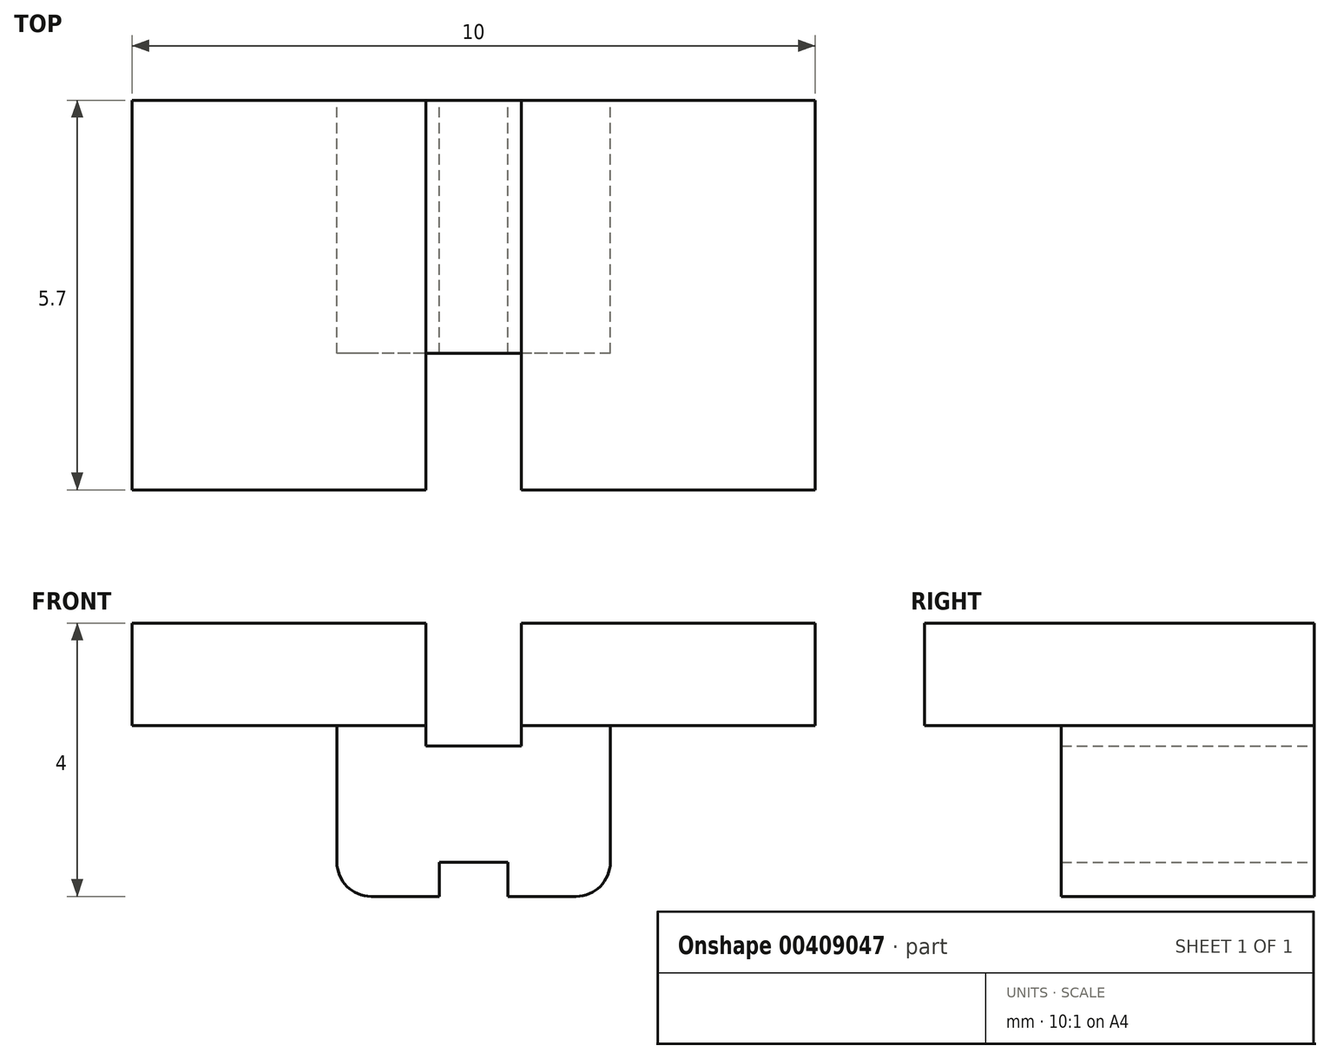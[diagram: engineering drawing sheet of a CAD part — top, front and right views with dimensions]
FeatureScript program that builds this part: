
annotation { "Feature Type Name" : "Feature", "Feature Type Description" : "" }
export const myFeature = defineFeature(function(context is Context, id is Id, definition is map)
    precondition{}
    {
        {
            var Q0;
            Q0=qCreatedBy(makeId("Top.planeOp"),FACE);
            var sketch = newSketch(context, id + "F0", { "sketchPlane" : qUnion([Q0])});
            skLineSegment(sketch, "E0.bottom", {"start": v(0.7, -0.75) * mm, "end": v(-0.7, -0.75) * mm});
            skLineSegment(sketch, "E0.top", {"start": v(0.7, 0.75) * mm, "end": v(-0.7, 0.75) * mm});
            skLineSegment(sketch, "E0.left", {"start": v(0.7, -0.75) * mm, "end": v(0.7, 0.75) * mm});
            skLineSegment(sketch, "E0.right", {"start": v(-0.7, -0.75) * mm, "end": v(-0.7, 0.75) * mm});
            skPoint(sketch, "E0.middle", {"position": v(0, 0) * mm});
            skLineSegment(sketch, "E1.bottom", {"start": v(2, -1.85) * mm, "end": v(-2, -1.85) * mm});
            skLineSegment(sketch, "E1.top", {"start": v(2, 1.85) * mm, "end": v(-2, 1.85) * mm});
            skLineSegment(sketch, "E1.left", {"start": v(2, -1.85) * mm, "end": v(2, 1.85) * mm});
            skLineSegment(sketch, "E1.right", {"start": v(-2, -1.85) * mm, "end": v(-2, 1.85) * mm});
            skLineSegment(sketch, "E2.bottom", {"start": v(5, -3.85) * mm, "end": v(-5, -3.85) * mm});
            skLineSegment(sketch, "E2.top", {"start": v(5, 1.85) * mm, "end": v(-5, 1.85) * mm});
            skLineSegment(sketch, "E2.left", {"start": v(5, -3.85) * mm, "end": v(5, 1.85) * mm});
            skLineSegment(sketch, "E2.right", {"start": v(-5, -3.85) * mm, "end": v(-5, 1.85) * mm});
            skPoint(sketch, "E2.middle", {"position": v(0, -1) * mm});
            skLineSegment(sketch, "E3", {"start": v(-0.7, -0.75) * mm, "end": v(-0.7, -3.85) * mm});
            skLineSegment(sketch, "E4", {"start": v(0.7, -0.75) * mm, "end": v(0.7, -3.85) * mm});
            skLineSegment(sketch, "E5", {"start": v(0.7, 0.75) * mm, "end": v(0.7, 1.85) * mm});
            skLineSegment(sketch, "E6", {"start": v(-0.7, 0.75) * mm, "end": v(-0.7, 1.85) * mm});
            skSolve(sketch);
        }
        {
            var Q0;
            Q0=makeQuery(id+"F0.imprint","IMPRINT",FACE,{"disambiguationData":[TD([[makeQuery(id+"F0.imprint","IMPRINT",EDGE,{"derivedFrom":sQuery(id+"F0.wireOp",EDGE,"E1.bottom")}),1.0]])]});
            var Q1;
            {var subQ0=sQuery(id+"F0.wireOp",EDGE,"E1.right");Q1=makeQuery(id+"F0.imprint","IMPRINT",FACE,{"disambiguationData":[TD([[makeQuery(id+"F0.imprint","IMPRINT",EDGE,{"derivedFrom":subQ0}),1.0]])]});}
            var Q2;
            {var subQ1=sQuery(id+"F0.wireOp",EDGE,"E1.left");Q2=makeQuery(id+"F0.imprint","IMPRINT",FACE,{"disambiguationData":[TD([[makeQuery(id+"F0.imprint","IMPRINT",EDGE,{"derivedFrom":subQ1}),-1.0]])]});}
            extrude(context, id + "F1", {"entities" : qUnion([Q0, Q1, Q2]), "oppositeDirection" : true, "depth" : 1.5 * mm});
        }
        {
            var Q0;
            Q0=makeQuery(id+"F0.imprint","IMPRINT",FACE,{"disambiguationData":[TD([[makeQuery(id+"F0.imprint","IMPRINT",EDGE,{"derivedFrom":sQuery(id+"F0.wireOp",EDGE,"E0.bottom")}),1.0]])]});
            var Q1;
            Q1=makeQuery(id+"F0.imprint","IMPRINT",FACE,{"disambiguationData":[TD([[makeQuery(id+"F0.imprint","IMPRINT",EDGE,{"derivedFrom":sQuery(id+"F0.wireOp",EDGE,"E0.bottom")}),-1.0]])]});
            var Q2;
            {var subQ6=sQuery(id+"F0.wireOp",EDGE,"E0.right");Q2=makeQuery(id+"F0.imprint","IMPRINT",FACE,{"disambiguationData":[TD([[makeQuery(id+"F0.imprint","IMPRINT",EDGE,{"derivedFrom":subQ6}),1.0]])]});}
            var Q3;
            Q3=makeQuery(id+"F0.imprint","IMPRINT",FACE,{"disambiguationData":[TD([[makeQuery(id+"F0.imprint","IMPRINT",EDGE,{"derivedFrom":sQuery(id+"F0.wireOp",EDGE,"E0.top")}),-1.0]])]});
            var Q4;
            {var subQ3=sQuery(id+"F0.wireOp",EDGE,"E0.left");Q4=makeQuery(id+"F0.imprint","IMPRINT",FACE,{"disambiguationData":[TD([[makeQuery(id+"F0.imprint","IMPRINT",EDGE,{"derivedFrom":subQ3}),-1.0]])]});}
            extrude(context, id + "F2", {"entities" : qUnion([Q0, Q1, Q2, Q3, Q4]), "operationType" : NewBodyOperationType.ADD, "oppositeDirection" : true, "depth" : 4 * mm});
        }
        {
            var Q0;
            Q0=makeQuery(id+"F0.imprint","IMPRINT",FACE,{"disambiguationData":[TD([[makeQuery(id+"F0.imprint","IMPRINT",EDGE,{"derivedFrom":sQuery(id+"F0.wireOp",EDGE,"E0.bottom")}),-1.0]])]});
            var Q1;
            Q1=makeQuery(id+"F0.imprint","IMPRINT",FACE,{"disambiguationData":[TD([[makeQuery(id+"F0.imprint","IMPRINT",EDGE,{"derivedFrom":sQuery(id+"F0.wireOp",EDGE,"E0.top")}),-1.0]])]});
            var Q2;
            {var subQ0=sQuery(id+"F0.wireOp",EDGE,"E0.bottom");Q2=makeQuery(id+"F0.imprint","IMPRINT",FACE,{"disambiguationData":[TD([[makeQuery(id+"F0.imprint","IMPRINT",EDGE,{"derivedFrom":subQ0}),1.0]])]});}
            var Q3;
            {var subQ0=sQuery(id+"F0.wireOp",EDGE,"E4");var subQ1=sQuery(id+"F0.wireOp",EDGE,"E1.bottom");var subQ2=makeQuery(id+"F0.imprint","INTERSECT",VERTEX,{"derivedFrom":[subQ1,subQ0]});Q3=makeQuery(id+"F0.imprint","IMPRINT",FACE,{"disambiguationData":[TD([[makeQuery(id+"F0.imprint","IMPRINT",EDGE,{"disambiguationData":[TD([[subQ2,-1.0]])],"derivedFrom":subQ1}),1.0]])]});}
            extrude(context, id + "F3", {"entities" : qUnion([Q0, Q1, Q2, Q3]), "operationType" : NewBodyOperationType.REMOVE, "oppositeDirection" : true, "depth" : 1.8 * mm});
        }
        {
            var Q0;
            Q0=makeQuery(id+"F2.opExtrude","CAP_FACE",FACE,{"disambiguationData":[OSD([sQuery(id+"F0.wireOp",EDGE,"E1.bottom"),sQuery(id+"F0.wireOp",EDGE,"E1.left"),sQuery(id+"F0.wireOp",EDGE,"E1.right"),sQuery(id+"F0.wireOp",EDGE,"E2.top")])],"isStart":false});
            var sketch = newSketch(context, id + "F4", { "sketchPlane" : qUnion([Q0])});
            skLineSegment(sketch, "E7.bottom", {"start": v(0.5, 2) * mm, "end": v(-0.5, 2) * mm});
            skLineSegment(sketch, "E7.top", {"start": v(0.5, -2) * mm, "end": v(-0.5, -2) * mm});
            skLineSegment(sketch, "E7.left", {"start": v(0.5, 2) * mm, "end": v(0.5, -2) * mm});
            skLineSegment(sketch, "E7.right", {"start": v(-0.5, 2) * mm, "end": v(-0.5, -2) * mm});
            skPoint(sketch, "E7.middle", {"position": v(0, 0) * mm});
            skSolve(sketch);
        }
        {
            var Q0;
            {var subQ0=sQuery(id+"F4.wireOp",EDGE,"E7.left");var subQ1=makeQuery(id+"F2.opExtrude","CAP_EDGE",EDGE,{"disambiguationData":[OSD([sQuery(id+"F0.wireOp",EDGE,"E1.bottom")])],"isStart":false});var subQ2=makeQuery(id+"F4.imprint","INTERSECT",VERTEX,{"derivedFrom":[subQ1,subQ0]});Q0=makeQuery(id+"F4.imprint","IMPRINT",FACE,{"disambiguationData":[TD([[makeQuery(id+"F4.imprint","IMPRINT",EDGE,{"disambiguationData":[TD([[subQ2,-1.0]])],"derivedFrom":subQ0}),-1.0]])]});}
            extrude(context, id + "F5", {"entities" : qUnion([Q0]), "operationType" : NewBodyOperationType.REMOVE, "oppositeDirection" : true, "depth" : 0.5 * mm});
        }
        {
            var Q0;
            Q0=makeQuery(id+"F2.opExtrude","CAP_EDGE",EDGE,{"disambiguationData":[OSD([sQuery(id+"F0.wireOp",EDGE,"E1.right")])],"isStart":false});
            var Q1;
            Q1=makeQuery(id+"F2.opExtrude","CAP_EDGE",EDGE,{"disambiguationData":[OSD([sQuery(id+"F0.wireOp",EDGE,"E1.left")])],"isStart":false});
            fillet(context, id + "F6", {"entities" : qUnion([Q0, Q1]), "radius" : 0.5 * mm, "tangentPropagation" : true, "allowEdgeOverflow" : false});
        }
    });
